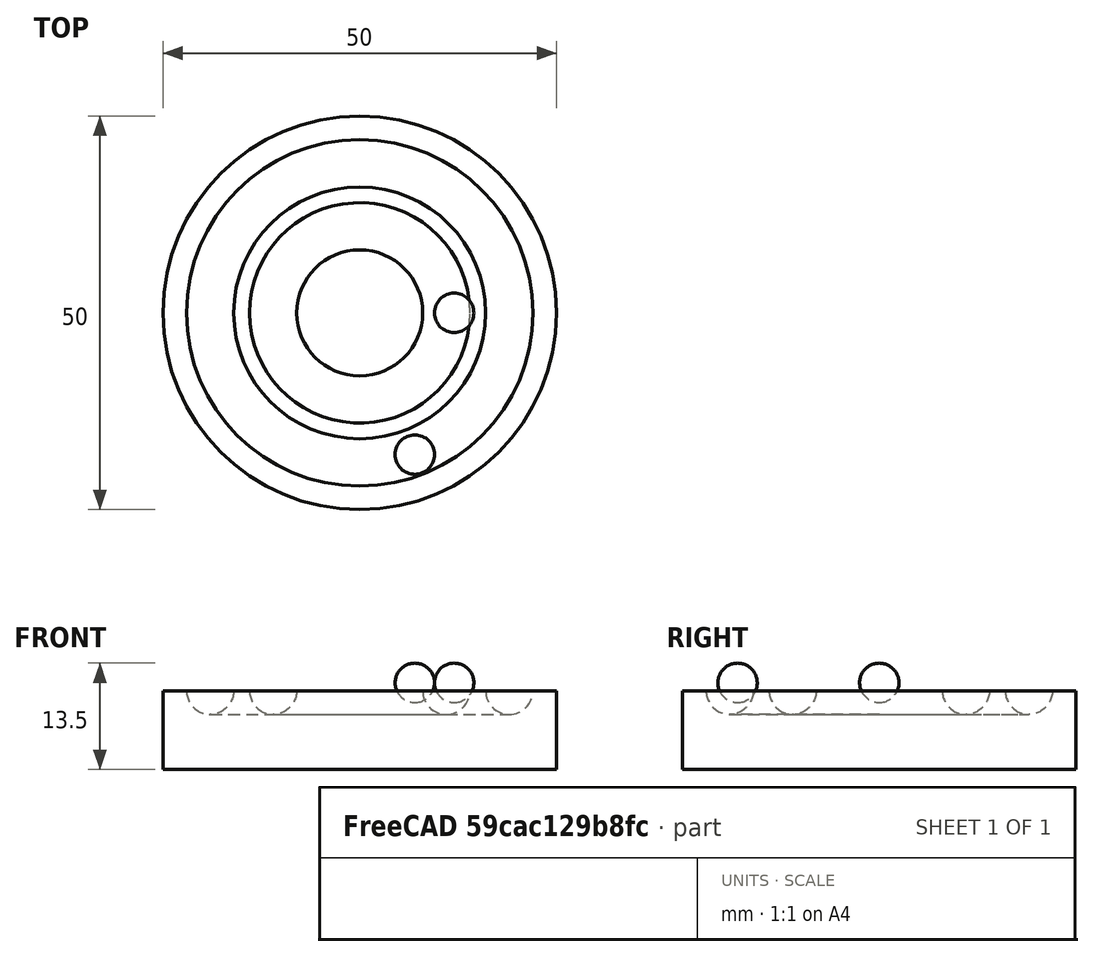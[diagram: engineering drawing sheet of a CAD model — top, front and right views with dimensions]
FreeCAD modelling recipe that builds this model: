
FCSTD DOCUMENT  (FreeCAD 0.21R33694 (Git))
Label: OJT1_T015R014_porta_caniques
License: All rights reserved
LicenseURL: http://en.wikipedia.org/wiki/All_rights_reserved
objects: Part::Torus×2, Part::Sphere×2, Part::Cylinder×1, Part::MultiFuse×1, Part::Cut×1
note: 7 computed .brp shape members not serialized (recipe doc carries the construction recipe); baked Part::Feature solids carry a one-line shape summary decoded from their .brp

FEATURE [Part::Cylinder] Cylinder
  Angle = 360
  AttacherType = Attacher::AttachEngine3D
  FirstAngle = 0
  Height = 10
  Radius = 25
  SecondAngle = 0
FEATURE [Part::Torus] Torus
  Angle1 = -180
  Angle2 = 180
  Angle3 = 360
  AttacherType = Attacher::AttachEngine3D
  Placement = pos=(0,0,10) rot=(0,0,1;0rad)
  Radius1 = 11
  Radius2 = 3
FEATURE [Part::Torus] Torus001
  Angle1 = -180
  Angle2 = 180
  Angle3 = 360
  AttacherType = Attacher::AttachEngine3D
  Placement = pos=(0,0,10) rot=(0,0,1;0rad)
  Radius1 = 19
  Radius2 = 3
FEATURE [Part::MultiFuse] Fusion
  Refine = true
  Shapes = -> [Torus,Torus001]
FEATURE [Part::Cut] Cut
  Base = -> Cylinder
  Refine = true
  Tool = -> Fusion
FEATURE [Part::Sphere] Sphere
  Angle1 = -90
  Angle2 = 90
  Angle3 = 360
  AttacherType = Attacher::AttachEngine3D
  Placement = pos=(12,0,11) rot=(0,0,1;0rad)
  Radius = 2.5
FEATURE [Part::Sphere] Sphere001
  Angle1 = -90
  Angle2 = 90
  Angle3 = 360
  AttacherType = Attacher::AttachEngine3D
  Placement = pos=(7,-18,11) rot=(0,0,1;0rad)
  Radius = 2.5
